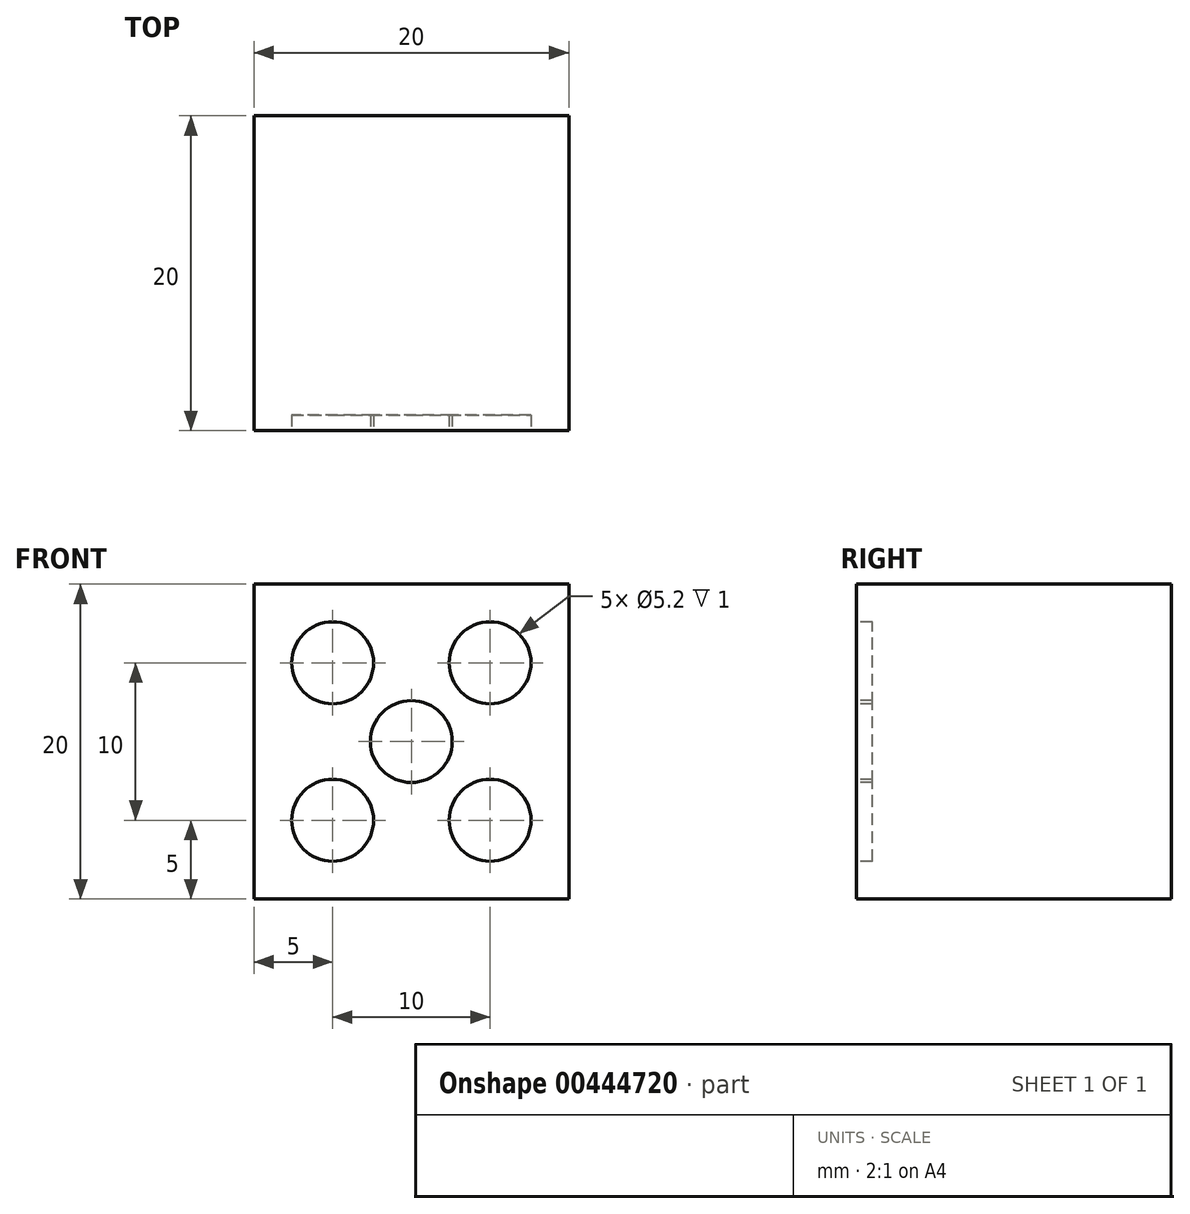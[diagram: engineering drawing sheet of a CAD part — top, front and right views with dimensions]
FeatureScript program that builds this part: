
annotation { "Feature Type Name" : "Feature", "Feature Type Description" : "" }
export const myFeature = defineFeature(function(context is Context, id is Id, definition is map)
    precondition{}
    {
        {
            var Q0;
            Q0=qCreatedBy(makeId("Front.planeOp"),FACE);
            var sketch = newSketch(context, id + "F0", { "sketchPlane" : qUnion([Q0])});
            skLineSegment(sketch, "E0.bottom", {"start": v(0, 0) * mm, "end": v(20, 0) * mm});
            skLineSegment(sketch, "E0.top", {"start": v(0, 20) * mm, "end": v(20, 20) * mm});
            skLineSegment(sketch, "E0.left", {"start": v(0, 0) * mm, "end": v(0, 20) * mm});
            skLineSegment(sketch, "E0.right", {"start": v(20, 0) * mm, "end": v(20, 20) * mm});
            skSolve(sketch);
        }
        {
            var Q0;
            Q0 = qSketchRegion(id + "F0", true);
            extrude(context, id + "F1", {"entities" : qUnion([Q0]), "depth" : 20 * mm});
        }
        {
            var Q0;
            Q0=makeQuery(id+"F1.opExtrude","CAP_FACE",FACE,{"disambiguationData":[OSD([sQuery(id+"F0.wireOp",EDGE,"E0.bottom"),sQuery(id+"F0.wireOp",EDGE,"E0.top"),sQuery(id+"F0.wireOp",EDGE,"E0.left"),sQuery(id+"F0.wireOp",EDGE,"E0.right")])],"isStart":false});
            var sketch = newSketch(context, id + "F2", { "sketchPlane" : qUnion([Q0])});
            skCircle(sketch, "E1", {"center": v(10, 10) * mm, "radius": 2.6 * mm});
            skCircle(sketch, "E2", {"center": v(5, 15) * mm, "radius": 2.6 * mm});
            skCircle(sketch, "E3", {"center": v(15, 15) * mm, "radius": 2.6 * mm});
            skCircle(sketch, "E4", {"center": v(15, 5) * mm, "radius": 2.6 * mm});
            skCircle(sketch, "E5", {"center": v(5, 5) * mm, "radius": 2.6 * mm});
            skPoint(sketch, "E6.orphan", {"position": v(0, 0) * mm});
            skPoint(sketch, "E7.start.orphan", {"position": v(20, 20) * mm});
            skSolve(sketch);
        }
        {
            var Q0;
            Q0=makeQuery(id+"F2.imprint","IMPRINT",FACE,{"disambiguationData":[TD([[makeQuery(id+"F2.imprint","IMPRINT",EDGE,{"derivedFrom":sQuery(id+"F2.wireOp",EDGE,"E1")}),1.0]])]});
            var Q1;
            Q1=makeQuery(id+"F2.imprint","IMPRINT",FACE,{"disambiguationData":[TD([[makeQuery(id+"F2.imprint","IMPRINT",EDGE,{"derivedFrom":sQuery(id+"F2.wireOp",EDGE,"E2")}),1.0]])]});
            var Q2;
            Q2=makeQuery(id+"F2.imprint","IMPRINT",FACE,{"disambiguationData":[TD([[makeQuery(id+"F2.imprint","IMPRINT",EDGE,{"derivedFrom":sQuery(id+"F2.wireOp",EDGE,"E3")}),1.0]])]});
            var Q3;
            Q3=makeQuery(id+"F2.imprint","IMPRINT",FACE,{"disambiguationData":[TD([[makeQuery(id+"F2.imprint","IMPRINT",EDGE,{"derivedFrom":sQuery(id+"F2.wireOp",EDGE,"E4")}),1.0]])]});
            var Q4;
            Q4=makeQuery(id+"F2.imprint","IMPRINT",FACE,{"disambiguationData":[TD([[makeQuery(id+"F2.imprint","IMPRINT",EDGE,{"derivedFrom":sQuery(id+"F2.wireOp",EDGE,"E5")}),1.0]])]});
            extrude(context, id + "F3", {"entities" : qUnion([Q0, Q1, Q2, Q3, Q4]), "operationType" : NewBodyOperationType.REMOVE, "oppositeDirection" : true, "depth" : 1 * mm});
        }
    });
